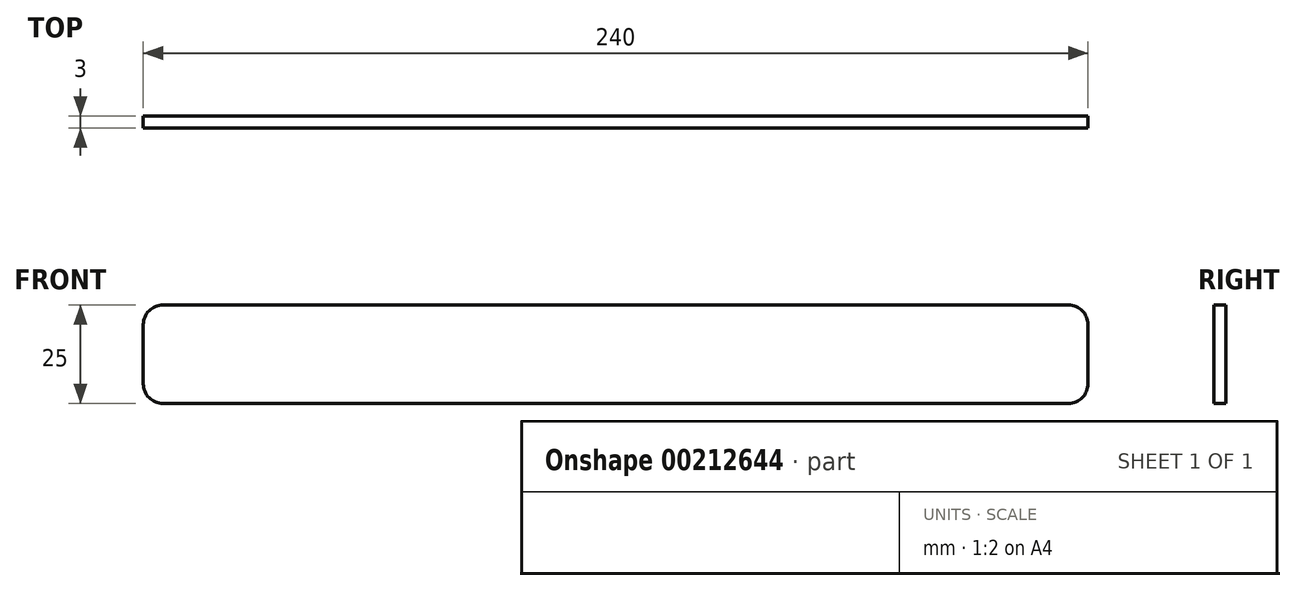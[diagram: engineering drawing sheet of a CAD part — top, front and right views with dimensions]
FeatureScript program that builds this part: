
annotation { "Feature Type Name" : "Feature", "Feature Type Description" : "" }
export const myFeature = defineFeature(function(context is Context, id is Id, definition is map)
    precondition{}
    {
        {
            var Q0;
            Q0=qCreatedBy(makeId("Front.planeOp"),FACE);
            var sketch = newSketch(context, id + "F0", { "sketchPlane" : qUnion([Q0])});
            skLineSegment(sketch, "E0.bottom", {"start": v(-120, 12.5) * mm, "end": v(120, 12.5) * mm});
            skLineSegment(sketch, "E0.top", {"start": v(-120, -12.5) * mm, "end": v(120, -12.5) * mm});
            skLineSegment(sketch, "E0.left", {"start": v(-120, 12.5) * mm, "end": v(-120, -12.5) * mm});
            skLineSegment(sketch, "E0.right", {"start": v(120, 12.5) * mm, "end": v(120, -12.5) * mm});
            skSolve(sketch);
        }
        {
            var Q0;
            Q0=qSketchRegion(id+"F0",true);
            extrude(context, id + "F1", {"entities" : qUnion([Q0]), "depth" : 3 * mm});
        }
        {
            var Q0;
            Q0=makeQuery(id+"F1.opExtrude","SWEPT_EDGE",EDGE,{"disambiguationData":[OSD([sQuery(id+"F0.wireOp",EDGE,"E0.bottom"),sQuery(id+"F0.wireOp",EDGE,"E0.left")])]});
            var Q1;
            Q1=makeQuery(id+"F1.opExtrude","SWEPT_EDGE",EDGE,{"disambiguationData":[OSD([sQuery(id+"F0.wireOp",EDGE,"E0.top"),sQuery(id+"F0.wireOp",EDGE,"E0.left")])]});
            var Q2;
            Q2=makeQuery(id+"F1.opExtrude","SWEPT_EDGE",EDGE,{"disambiguationData":[OSD([sQuery(id+"F0.wireOp",EDGE,"E0.bottom"),sQuery(id+"F0.wireOp",EDGE,"E0.right")])]});
            var Q3;
            Q3=makeQuery(id+"F1.opExtrude","SWEPT_EDGE",EDGE,{"disambiguationData":[OSD([sQuery(id+"F0.wireOp",EDGE,"E0.top"),sQuery(id+"F0.wireOp",EDGE,"E0.right")])]});
            fillet(context, id + "F2", {"entities" : qUnion([Q0, Q1, Q2, Q3]), "radius" : 5 * mm, "tangentPropagation" : true, "allowEdgeOverflow" : false});
        }
    });
